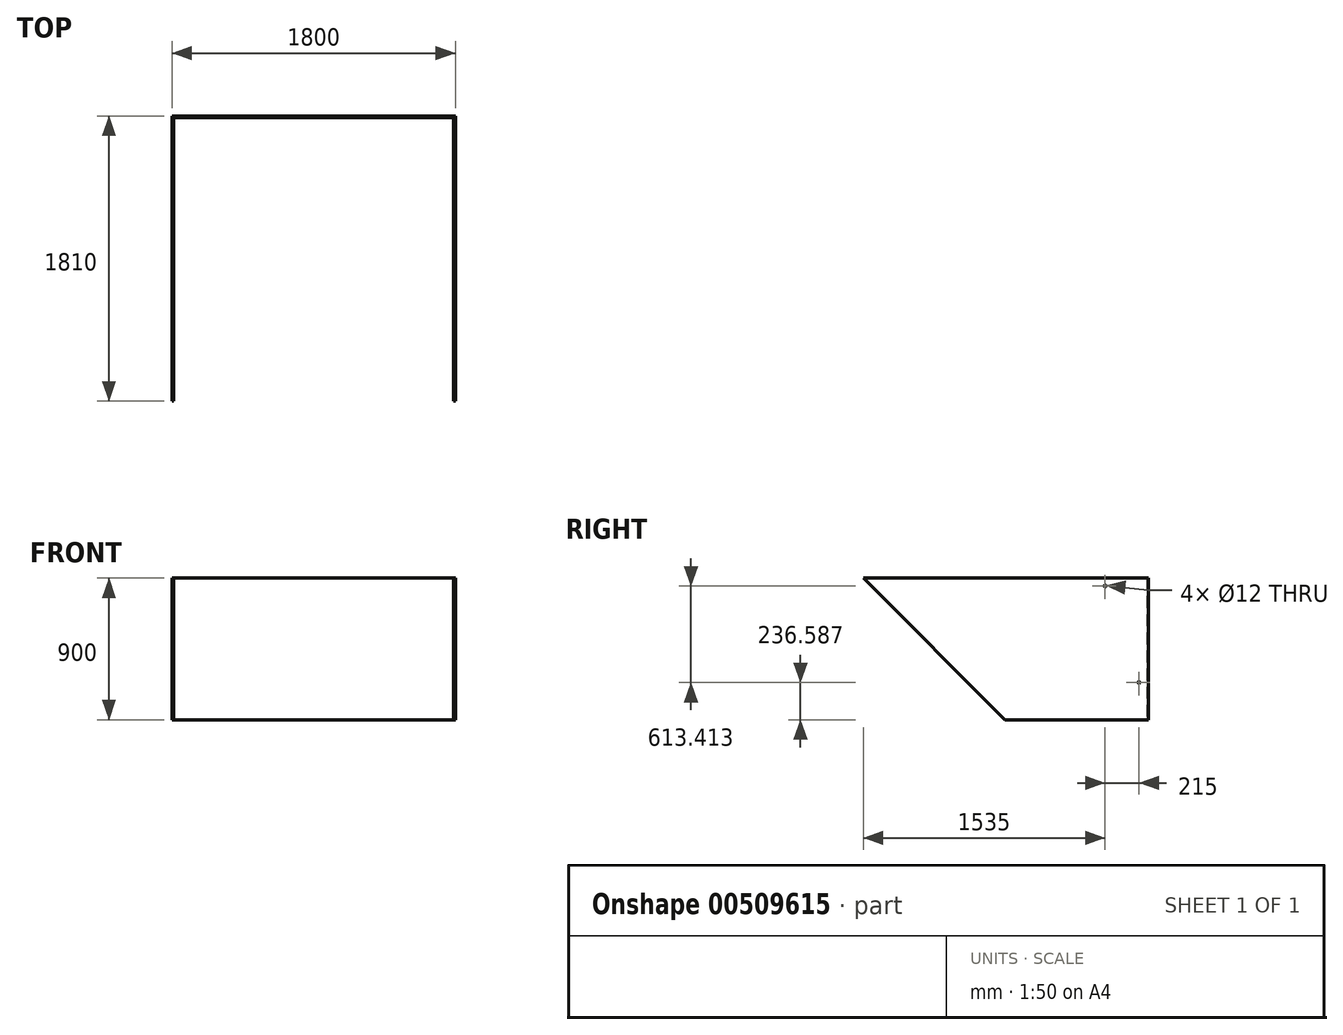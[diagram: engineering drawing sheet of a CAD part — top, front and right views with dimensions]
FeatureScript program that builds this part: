
annotation { "Feature Type Name" : "Feature", "Feature Type Description" : "" }
export const myFeature = defineFeature(function(context is Context, id is Id, definition is map)
    precondition{}
    {
        {
            var Q0;
            Q0=qCreatedBy(makeId("Front.planeOp"),FACE);
            var sketch = newSketch(context, id + "F0", { "sketchPlane" : qUnion([Q0])});
            skLineSegment(sketch, "E0.bottom", {"start": v(-900, 450) * mm, "end": v(900, 450) * mm});
            skLineSegment(sketch, "E0.top", {"start": v(-900, -450) * mm, "end": v(900, -450) * mm});
            skLineSegment(sketch, "E0.left", {"start": v(-900, 450) * mm, "end": v(-900, -450) * mm});
            skLineSegment(sketch, "E0.right", {"start": v(900, 450) * mm, "end": v(900, -450) * mm});
            skPoint(sketch, "E0.middle", {"position": v(0, 0) * mm});
            skSolve(sketch);
        }
        {
            var Q0;
            Q0=makeQuery(id+"F0.imprint","IMPRINT",FACE,{"disambiguationData":[TD([[makeQuery(id+"F0.imprint","IMPRINT",EDGE,{"derivedFrom":sQuery(id+"F0.wireOp",EDGE,"E0.bottom")}),-1.0]])]});
            extrude(context, id + "F1", {"entities" : qUnion([Q0]), "endBound" : BoundingType.SYMMETRIC, "depth" : 10 * mm});
        }
        {
            var Q0;
            Q0=makeQuery(id+"F1.opExtrude","CAP_FACE",FACE,{"disambiguationData":[OSD([sQuery(id+"F0.wireOp",EDGE,"E0.bottom"),sQuery(id+"F0.wireOp",EDGE,"E0.top"),sQuery(id+"F0.wireOp",EDGE,"E0.left"),sQuery(id+"F0.wireOp",EDGE,"E0.right")])],"isStart":false});
            var sketch = newSketch(context, id + "F2", { "sketchPlane" : qUnion([Q0])});
            skLineSegment(sketch, "E1.bottom", {"start": v(900, 450) * mm, "end": v(890, 450) * mm});
            skLineSegment(sketch, "E1.top", {"start": v(900, -450) * mm, "end": v(890, -450) * mm});
            skLineSegment(sketch, "E1.left", {"start": v(900, 450) * mm, "end": v(900, -450) * mm});
            skLineSegment(sketch, "E1.right", {"start": v(890, 450) * mm, "end": v(890, -450) * mm});
            skLineSegment(sketch, "E2.bottom", {"start": v(-900, 450) * mm, "end": v(-890, 450) * mm});
            skLineSegment(sketch, "E2.top", {"start": v(-900, -450) * mm, "end": v(-890, -450) * mm});
            skLineSegment(sketch, "E2.left", {"start": v(-900, 450) * mm, "end": v(-900, -450) * mm});
            skLineSegment(sketch, "E2.right", {"start": v(-890, 450) * mm, "end": v(-890, -450) * mm});
            skSolve(sketch);
        }
        {
            var Q0;
            Q0=makeQuery(id+"F2.imprint","IMPRINT",FACE,{"disambiguationData":[TD([[makeQuery(id+"F2.imprint","IMPRINT",EDGE,{"derivedFrom":sQuery(id+"F2.wireOp",EDGE,"E2.bottom")}),-1.0]])]});
            var Q1;
            Q1=makeQuery(id+"F2.imprint","IMPRINT",FACE,{"disambiguationData":[TD([[makeQuery(id+"F2.imprint","IMPRINT",EDGE,{"derivedFrom":sQuery(id+"F2.wireOp",EDGE,"E1.bottom")}),-1.0]])]});
            extrude(context, id + "F3", {"entities" : qUnion([Q0, Q1]), "operationType" : NewBodyOperationType.ADD, "depth" : 1800 * mm});
        }
        {
            var Q0;
            Q0=makeQuery(id+"F3.boolean.opBoolean","MERGE",FACE,{"derivedFrom":[makeQuery(id+"F1.opExtrude","SWEPT_FACE",FACE,{"disambiguationData":[OSD([sQuery(id+"F0.wireOp",EDGE,"E0.right")])]}),makeQuery(id+"F3.opExtrude","SWEPT_FACE",FACE,{"disambiguationData":[OSD([sQuery(id+"F2.wireOp",EDGE,"E1.left")])]})]});
            var sketch = newSketch(context, id + "F4", { "sketchPlane" : qUnion([Q0])});
            skLineSegment(sketch, "E3", {"start": v(-1805, 450) * mm, "end": v(-1805, -450) * mm});
            skLineSegment(sketch, "E4", {"start": v(-1805, -450) * mm, "end": v(-905, -450) * mm});
            skLineSegment(sketch, "E5", {"start": v(-905, -450) * mm, "end": v(-1805, 450) * mm});
            skSolve(sketch);
        }
        {
            var Q0;
            Q0=makeQuery(id+"F4.imprint","IMPRINT",FACE,{"disambiguationData":[TD([[makeQuery(id+"F4.imprint","IMPRINT",EDGE,{"derivedFrom":sQuery(id+"F4.wireOp",EDGE,"E3")}),1.0]])]});
            extrude(context, id + "F5", {"entities" : qUnion([Q0]), "operationType" : NewBodyOperationType.REMOVE, "endBound" : BoundingType.THROUGH_ALL, "oppositeDirection" : true, "depth" : 25 * mm});
        }
        {
            var Q0;
            Q0=makeQuery(id+"F3.boolean.opBoolean","MERGE",FACE,{"derivedFrom":[makeQuery(id+"F1.opExtrude","SWEPT_FACE",FACE,{"disambiguationData":[OSD([sQuery(id+"F0.wireOp",EDGE,"E0.left")])]}),makeQuery(id+"F3.opExtrude","SWEPT_FACE",FACE,{"disambiguationData":[OSD([sQuery(id+"F2.wireOp",EDGE,"E2.left")])]})]});
            var sketch = newSketch(context, id + "F6", { "sketchPlane" : qUnion([Q0])});
            skLineSegment(sketch, "E6", {"start": v(-5, 450) * mm, "end": v(270, 450) * mm});
            skLineSegment(sketch, "E7", {"start": v(270, 450) * mm, "end": v(270, 400) * mm});
            skPoint(sketch, "E8", {"position": v(270, 400) * mm});
            skLineSegment(sketch, "E9", {"start": v(-5, -450) * mm, "end": v(55, -450) * mm, "construction": true});
            skLineSegment(sketch, "E10", {"start": v(55, -450) * mm, "end": v(55, 450) * mm, "construction": true});
            skLineSegment(sketch, "E11", {"start": v(270, 400) * mm, "end": v(55, -213.41) * mm});
            skPoint(sketch, "E12", {"position": v(55, -213.41) * mm});
            skSolve(sketch);
        }
        {
            var Q0;
            Q0=sQuery(id+"F6.wireOp",VERTEX,"E8");
            var Q1;
            Q1=sQuery(id+"F6.wireOp",VERTEX,"E12");
            var Q2;
            Q2=makeQuery(id+"F1.opExtrude","SWEPT_BODY",BODY,{"disambiguationData":[OSD([sQuery(id+"F0.wireOp",EDGE,"E0.bottom"),sQuery(id+"F0.wireOp",EDGE,"E0.top"),sQuery(id+"F0.wireOp",EDGE,"E0.left"),sQuery(id+"F0.wireOp",EDGE,"E0.right")])]});
            hole(context, id + "F7", {"style" : HoleStyle.SIMPLE, "endStyle" : HoleEndStyle.THROUGH, "holeDiameter" : 12 * mm, "isTappedThrough" : true, "tappedDepth" : 12 * mm, "tapClearance" : 3, "locations" : qUnion([Q0, Q1]), "scope" : qUnion([Q2])});
        }
    });
